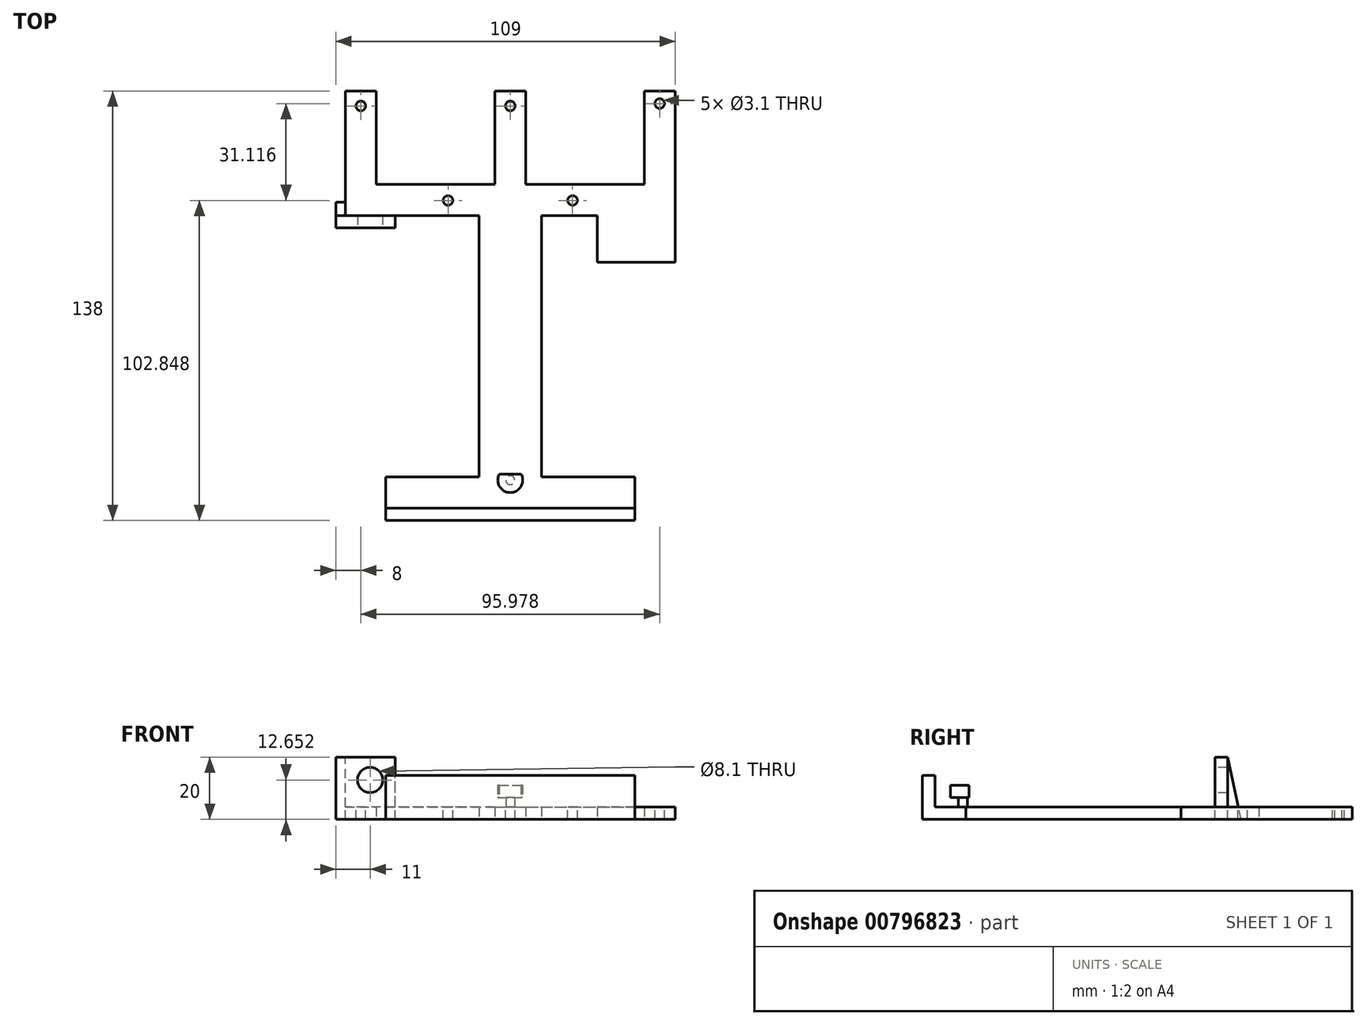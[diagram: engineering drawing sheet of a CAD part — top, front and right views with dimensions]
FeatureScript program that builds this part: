
annotation { "Feature Type Name" : "Feature", "Feature Type Description" : "" }
export const myFeature = defineFeature(function(context is Context, id is Id, definition is map)
    precondition{}
    {
        {
            var Q0;
            Q0=qCreatedBy(makeId("Top.planeOp"),FACE);
            var sketch = newSketch(context, id + "F0", { "sketchPlane" : qUnion([Q0])});
            skLineSegment(sketch, "E0.bottom", {"start": v(-10, 52) * mm, "end": v(10, 52) * mm});
            skLineSegment(sketch, "E0.top", {"start": v(-10, -52) * mm, "end": v(10, -52) * mm});
            skLineSegment(sketch, "E0.left", {"start": v(-10, 52) * mm, "end": v(-10, -52) * mm});
            skLineSegment(sketch, "E0.right", {"start": v(10, 52) * mm, "end": v(10, -52) * mm});
            skPoint(sketch, "E0.middle", {"position": v(0, 0) * mm});
            skLineSegment(sketch, "E1.bottom", {"start": v(10, 52) * mm, "end": v(53, 52) * mm});
            skLineSegment(sketch, "E1.top", {"start": v(10, 42) * mm, "end": v(53, 42) * mm});
            skLineSegment(sketch, "E1.left", {"start": v(10, 52) * mm, "end": v(10, 42) * mm});
            skLineSegment(sketch, "E1.right", {"start": v(53, 52) * mm, "end": v(53, 42) * mm});
            skLineSegment(sketch, "E2.bottom", {"start": v(-10, 52) * mm, "end": v(-53, 52) * mm});
            skLineSegment(sketch, "E2.top", {"start": v(-10, 42) * mm, "end": v(-53, 42) * mm});
            skLineSegment(sketch, "E2.left", {"start": v(-10, 52) * mm, "end": v(-10, 42) * mm});
            skLineSegment(sketch, "E2.right", {"start": v(-53, 52) * mm, "end": v(-53, 42) * mm});
            skLineSegment(sketch, "E3.bottom", {"start": v(10, -52) * mm, "end": v(40, -52) * mm});
            skLineSegment(sketch, "E3.top", {"start": v(10, -42) * mm, "end": v(40, -42) * mm});
            skLineSegment(sketch, "E3.left", {"start": v(10, -52) * mm, "end": v(10, -42) * mm});
            skLineSegment(sketch, "E3.right", {"start": v(40, -52) * mm, "end": v(40, -42) * mm});
            skLineSegment(sketch, "E4.bottom", {"start": v(-10, -52) * mm, "end": v(-40, -52) * mm});
            skLineSegment(sketch, "E4.top", {"start": v(-10, -42) * mm, "end": v(-40, -42) * mm});
            skLineSegment(sketch, "E4.left", {"start": v(-10, -52) * mm, "end": v(-10, -42) * mm});
            skLineSegment(sketch, "E4.right", {"start": v(-40, -52) * mm, "end": v(-40, -42) * mm});
            skLineSegment(sketch, "E5.bottom", {"start": v(-53, 52) * mm, "end": v(53, 52) * mm});
            skLineSegment(sketch, "E5.top", {"start": v(-53, 82) * mm, "end": v(53, 82) * mm});
            skLineSegment(sketch, "E5.left", {"start": v(-53, 52) * mm, "end": v(-53, 82) * mm});
            skLineSegment(sketch, "E5.right", {"start": v(53, 52) * mm, "end": v(53, 82) * mm});
            skLineSegment(sketch, "E6.bottom", {"start": v(53, 42) * mm, "end": v(28, 42) * mm});
            skLineSegment(sketch, "E6.top", {"start": v(53, 27) * mm, "end": v(28, 27) * mm});
            skLineSegment(sketch, "E6.left", {"start": v(53, 42) * mm, "end": v(53, 27) * mm});
            skLineSegment(sketch, "E6.right", {"start": v(28, 42) * mm, "end": v(28, 27) * mm});
            skLineSegment(sketch, "E7.bottom", {"start": v(-53, 52) * mm, "end": v(-43, 52) * mm});
            skLineSegment(sketch, "E7.top", {"start": v(-53, 82) * mm, "end": v(-43, 82) * mm});
            skLineSegment(sketch, "E7.right", {"start": v(-43, 52) * mm, "end": v(-43, 82) * mm});
            skLineSegment(sketch, "E8.bottom", {"start": v(53, 52) * mm, "end": v(43, 52) * mm});
            skLineSegment(sketch, "E8.top", {"start": v(53, 82) * mm, "end": v(43, 82) * mm});
            skLineSegment(sketch, "E8.right", {"start": v(43, 52) * mm, "end": v(43, 82) * mm});
            skLineSegment(sketch, "E9.bottom", {"start": v(0, 52) * mm, "end": v(5, 52) * mm});
            skLineSegment(sketch, "E9.top", {"start": v(0, 82) * mm, "end": v(5, 82) * mm});
            skLineSegment(sketch, "E9.left", {"start": v(0, 52) * mm, "end": v(0, 82) * mm});
            skLineSegment(sketch, "E9.right", {"start": v(5, 52) * mm, "end": v(5, 82) * mm});
            skLineSegment(sketch, "E10.bottom", {"start": v(0, 52) * mm, "end": v(-5, 52) * mm});
            skLineSegment(sketch, "E10.top", {"start": v(0, 82) * mm, "end": v(-5, 82) * mm});
            skLineSegment(sketch, "E10.right", {"start": v(-5, 52) * mm, "end": v(-5, 82) * mm});
            skSolve(sketch);
        }
        {
            var Q0;
            {var subQ0=sQuery(id+"F0.wireOp",EDGE,"E5.left");Q0=makeQuery(id+"F0.imprint","IMPRINT",FACE,{"disambiguationData":[TD([[makeQuery(id+"F0.imprint","IMPRINT",EDGE,{"derivedFrom":subQ0}),-1.0]])]});}
            var Q1;
            {var subQ0=sQuery(id+"F0.wireOp",EDGE,"E2.top");Q1=makeQuery(id+"F0.imprint","IMPRINT",FACE,{"disambiguationData":[TD([[makeQuery(id+"F0.imprint","IMPRINT",EDGE,{"derivedFrom":subQ0}),-1.0]])]});}
            var Q2;
            {var subQ2=sQuery(id+"F0.wireOp",EDGE,"E9.left");Q2=makeQuery(id+"F0.imprint","IMPRINT",FACE,{"disambiguationData":[TD([[makeQuery(id+"F0.imprint","IMPRINT",EDGE,{"derivedFrom":subQ2}),1.0]])]});}
            var Q3;
            {var subQ2=sQuery(id+"F0.wireOp",EDGE,"E9.left");Q3=makeQuery(id+"F0.imprint","IMPRINT",FACE,{"disambiguationData":[TD([[makeQuery(id+"F0.imprint","IMPRINT",EDGE,{"derivedFrom":subQ2}),-1.0]])]});}
            var Q4;
            {var subQ6=sQuery(id+"F0.wireOp",EDGE,"E0.top");Q4=makeQuery(id+"F0.imprint","IMPRINT",FACE,{"disambiguationData":[TD([[makeQuery(id+"F0.imprint","IMPRINT",EDGE,{"derivedFrom":subQ6}),1.0]])]});}
            var Q5;
            {var subQ0=sQuery(id+"F0.wireOp",EDGE,"E4.bottom");Q5=makeQuery(id+"F0.imprint","IMPRINT",FACE,{"disambiguationData":[TD([[makeQuery(id+"F0.imprint","IMPRINT",EDGE,{"derivedFrom":subQ0}),-1.0]])]});}
            var Q6;
            {var subQ0=sQuery(id+"F0.wireOp",EDGE,"E3.bottom");Q6=makeQuery(id+"F0.imprint","IMPRINT",FACE,{"disambiguationData":[TD([[makeQuery(id+"F0.imprint","IMPRINT",EDGE,{"derivedFrom":subQ0}),1.0]])]});}
            var Q7;
            Q7=makeQuery(id+"F0.imprint","IMPRINT",FACE,{"disambiguationData":[TD([[makeQuery(id+"F0.imprint","IMPRINT",EDGE,{"derivedFrom":sQuery(id+"F0.wireOp",EDGE,"E6.top")}),-1.0]])]});
            var Q8;
            {var subQ1=sQuery(id+"F0.wireOp",EDGE,"E1.bottom");Q8=makeQuery(id+"F0.imprint","IMPRINT",FACE,{"disambiguationData":[TD([[makeQuery(id+"F0.imprint","IMPRINT",EDGE,{"derivedFrom":subQ1}),-1.0]])]});}
            var Q9;
            {var subQ0=sQuery(id+"F0.wireOp",EDGE,"E5.right");Q9=makeQuery(id+"F0.imprint","IMPRINT",FACE,{"disambiguationData":[TD([[makeQuery(id+"F0.imprint","IMPRINT",EDGE,{"derivedFrom":subQ0}),1.0]])]});}
            var Q10;
            {var subQ2=sQuery(id+"F0.wireOp",EDGE,"E1.right");Q10=makeQuery(id+"F0.imprint","IMPRINT",FACE,{"disambiguationData":[TD([[makeQuery(id+"F0.imprint","IMPRINT",EDGE,{"derivedFrom":subQ2}),-1.0]])]});}
            extrude(context, id + "F1", {"entities" : qUnion([Q0, Q1, Q2, Q3, Q4, Q5, Q6, Q7, Q8, Q9, Q10]), "depth" : 4 * mm, "offsetDistance" : 25 * mm});
        }
        {
            var Q0;
            Q0=makeQuery(id+"F1.opExtrude","SWEPT_FACE",FACE,{"disambiguationData":[OSD([sQuery(id+"F0.wireOp",EDGE,"E2.top")])]});
            var sketch = newSketch(context, id + "F2", { "sketchPlane" : qUnion([Q0])});
            skLineSegment(sketch, "E11.bottom", {"start": v(-53, 0) * mm, "end": v(-37, 0) * mm});
            skLineSegment(sketch, "E11.top", {"start": v(-53, 20) * mm, "end": v(-37, 20) * mm});
            skLineSegment(sketch, "E11.left", {"start": v(-53, 0) * mm, "end": v(-53, 20) * mm});
            skLineSegment(sketch, "E11.right", {"start": v(-37, 0) * mm, "end": v(-37, 20) * mm});
            skSolve(sketch);
        }
        {
            var Q0;
            {var subQ0=sQuery(id+"F2.wireOp",EDGE,"E11.top");Q0=makeQuery(id+"F2.imprint","IMPRINT",FACE,{"disambiguationData":[TD([[makeQuery(id+"F2.imprint","IMPRINT",EDGE,{"derivedFrom":subQ0}),-1.0]])]});}
            var Q1;
            {var subQ0=sQuery(id+"F2.wireOp",EDGE,"E11.bottom");Q1=makeQuery(id+"F2.imprint","IMPRINT",FACE,{"disambiguationData":[TD([[makeQuery(id+"F2.imprint","IMPRINT",EDGE,{"derivedFrom":subQ0}),-1.0]])]});}
            extrude(context, id + "F3", {"entities" : qUnion([Q0, Q1]), "operationType" : NewBodyOperationType.ADD, "depth" : 4 * mm, "offsetDistance" : 25 * mm});
        }
        {
            var Q0;
            Q0=makeQuery(id+"F3.opExtrude","CAP_FACE",FACE,{"disambiguationData":[OSD([sQuery(id+"F2.wireOp",EDGE,"E11.bottom"),sQuery(id+"F2.wireOp",EDGE,"E11.top"),sQuery(id+"F2.wireOp",EDGE,"E11.left"),sQuery(id+"F2.wireOp",EDGE,"E11.right")])],"isStart":false});
            var sketch = newSketch(context, id + "F4", { "sketchPlane" : qUnion([Q0])});
            skCircle(sketch, "E12", {"center": v(-45, 12.65) * mm, "radius": 4.07 * mm});
            skPoint(sketch, "E12.centerSnap0", {"position": v(-45, 20) * mm});
            skSolve(sketch);
        }
        {
            var Q0;
            Q0=sQuery(id+"F4.wireOp",VERTEX,"E12.center");
            var Q1;
            Q1=makeQuery(id+"F1.opExtrude","SWEPT_BODY",BODY,{"disambiguationData":[OSD([sQuery(id+"F0.wireOp",EDGE,"E0.bottom"),sQuery(id+"F0.wireOp",EDGE,"E0.top"),sQuery(id+"F0.wireOp",EDGE,"E0.left"),sQuery(id+"F0.wireOp",EDGE,"E0.right"),sQuery(id+"F0.wireOp",EDGE,"E1.bottom"),sQuery(id+"F0.wireOp",EDGE,"E1.top"),sQuery(id+"F0.wireOp",EDGE,"E1.right"),sQuery(id+"F0.wireOp",EDGE,"E2.bottom"),sQuery(id+"F0.wireOp",EDGE,"E2.top"),sQuery(id+"F0.wireOp",EDGE,"E2.right"),sQuery(id+"F0.wireOp",EDGE,"E3.bottom"),sQuery(id+"F0.wireOp",EDGE,"E3.top"),sQuery(id+"F0.wireOp",EDGE,"E3.right"),sQuery(id+"F0.wireOp",EDGE,"E4.bottom"),sQuery(id+"F0.wireOp",EDGE,"E4.top"),sQuery(id+"F0.wireOp",EDGE,"E4.right"),sQuery(id+"F0.wireOp",EDGE,"E5.top"),sQuery(id+"F0.wireOp",EDGE,"E5.left"),sQuery(id+"F0.wireOp",EDGE,"E5.right"),sQuery(id+"F0.wireOp",EDGE,"E6.top"),sQuery(id+"F0.wireOp",EDGE,"E6.left"),sQuery(id+"F0.wireOp",EDGE,"E6.right"),sQuery(id+"F0.wireOp",EDGE,"E7.right"),sQuery(id+"F0.wireOp",EDGE,"E8.right"),sQuery(id+"F0.wireOp",EDGE,"E9.right"),sQuery(id+"F0.wireOp",EDGE,"E10.right")])]});
            hole(context, id + "F5", {"style" : HoleStyle.SIMPLE, "endStyle" : HoleEndStyle.THROUGH, "holeDiameter" : 8.1 * mm, "majorDiameter" : 5 * mm, "isTappedThrough" : true, "tappedDepth" : 12 * mm, "tapClearance" : 3, "locations" : qUnion([Q0]), "scope" : qUnion([Q1])});
        }
        {
            var Q0;
            Q0=makeQuery(id+"F3.boolean.opBoolean","MERGE",FACE,{"derivedFrom":[makeQuery(id+"F1.opExtrude","SWEPT_FACE",FACE,{"disambiguationData":[OSD([sQuery(id+"F0.wireOp",EDGE,"E2.right"),sQuery(id+"F0.wireOp",EDGE,"E5.left")])]}),makeQuery(id+"F3.opExtrude","SWEPT_FACE",FACE,{"disambiguationData":[OSD([sQuery(id+"F2.wireOp",EDGE,"E11.left")])]})]});
            var sketch = newSketch(context, id + "F6", { "sketchPlane" : qUnion([Q0])});
            skLineSegment(sketch, "E13", {"start": v(-46.34, 0) * mm, "end": v(-42, 20) * mm});
            skLineSegment(sketch, "E14", {"start": v(-42, 20) * mm, "end": v(-38, 20) * mm});
            skLineSegment(sketch, "E15", {"start": v(-38, 20) * mm, "end": v(-38, 0) * mm});
            skLineSegment(sketch, "E16", {"start": v(-38, 0) * mm, "end": v(-46.34, 0) * mm});
            skSolve(sketch);
        }
        {
            var Q0;
            {var subQ1=makeQuery(id+"F3.opExtrude","CAP_EDGE",EDGE,{"disambiguationData":[OSD([sQuery(id+"F2.wireOp",EDGE,"E11.left")])],"isStart":true});Q0=makeQuery(id+"F6.imprint","IMPRINT",FACE,{"disambiguationData":[TD([[makeQuery(id+"F6.imprint","IMPRINT",EDGE,{"derivedFrom":subQ1}),1.0]])]});}
            var Q1;
            Q1=makeQuery(id+"F6.imprint","IMPRINT",FACE,{"disambiguationData":[TD([[makeQuery(id+"F6.imprint","IMPRINT",EDGE,{"derivedFrom":sQuery(id+"F6.wireOp",EDGE,"E14")}),1.0]])]});
            extrude(context, id + "F7", {"entities" : qUnion([Q0, Q1]), "operationType" : NewBodyOperationType.ADD, "depth" : 3 * mm, "offsetDistance" : 25 * mm});
        }
        {
            var Q0;
            Q0=makeQuery(id+"F1.opExtrude","SWEPT_FACE",FACE,{"disambiguationData":[OSD([sQuery(id+"F0.wireOp",EDGE,"E0.top"),sQuery(id+"F0.wireOp",EDGE,"E3.bottom"),sQuery(id+"F0.wireOp",EDGE,"E4.bottom")])]});
            var sketch = newSketch(context, id + "F8", { "sketchPlane" : qUnion([Q0])});
            skLineSegment(sketch, "E17.bottom", {"start": v(-40, 0) * mm, "end": v(40, 0) * mm});
            skLineSegment(sketch, "E17.top", {"start": v(-40, 14.08) * mm, "end": v(40, 14.08) * mm});
            skLineSegment(sketch, "E17.left", {"start": v(-40, 0) * mm, "end": v(-40, 14.08) * mm});
            skLineSegment(sketch, "E17.right", {"start": v(40, 0) * mm, "end": v(40, 14.08) * mm});
            skSolve(sketch);
        }
        {
            var Q0;
            {var subQ0=sQuery(id+"F8.wireOp",EDGE,"E17.top");Q0=makeQuery(id+"F8.imprint","IMPRINT",FACE,{"disambiguationData":[TD([[makeQuery(id+"F8.imprint","IMPRINT",EDGE,{"derivedFrom":subQ0}),-1.0]])]});}
            var Q1;
            {var subQ0=sQuery(id+"F8.wireOp",EDGE,"E17.bottom");Q1=makeQuery(id+"F8.imprint","IMPRINT",FACE,{"disambiguationData":[TD([[makeQuery(id+"F8.imprint","IMPRINT",EDGE,{"derivedFrom":subQ0}),1.0]])]});}
            extrude(context, id + "F9", {"entities" : qUnion([Q0, Q1]), "operationType" : NewBodyOperationType.ADD, "depth" : 4 * mm, "offsetDistance" : 25 * mm});
        }
        {
            var Q0;
            Q0=makeQuery(id+"F1.opExtrude","CAP_FACE",FACE,{"disambiguationData":[OSD([sQuery(id+"F0.wireOp",EDGE,"E0.bottom"),sQuery(id+"F0.wireOp",EDGE,"E0.top"),sQuery(id+"F0.wireOp",EDGE,"E0.left"),sQuery(id+"F0.wireOp",EDGE,"E0.right"),sQuery(id+"F0.wireOp",EDGE,"E1.bottom"),sQuery(id+"F0.wireOp",EDGE,"E1.top"),sQuery(id+"F0.wireOp",EDGE,"E1.right"),sQuery(id+"F0.wireOp",EDGE,"E2.bottom"),sQuery(id+"F0.wireOp",EDGE,"E2.top"),sQuery(id+"F0.wireOp",EDGE,"E2.right"),sQuery(id+"F0.wireOp",EDGE,"E3.bottom"),sQuery(id+"F0.wireOp",EDGE,"E3.top"),sQuery(id+"F0.wireOp",EDGE,"E3.right"),sQuery(id+"F0.wireOp",EDGE,"E4.bottom"),sQuery(id+"F0.wireOp",EDGE,"E4.top"),sQuery(id+"F0.wireOp",EDGE,"E4.right"),sQuery(id+"F0.wireOp",EDGE,"E5.top"),sQuery(id+"F0.wireOp",EDGE,"E5.left"),sQuery(id+"F0.wireOp",EDGE,"E5.right"),sQuery(id+"F0.wireOp",EDGE,"E6.top"),sQuery(id+"F0.wireOp",EDGE,"E6.left"),sQuery(id+"F0.wireOp",EDGE,"E6.right"),sQuery(id+"F0.wireOp",EDGE,"E7.right"),sQuery(id+"F0.wireOp",EDGE,"E8.right"),sQuery(id+"F0.wireOp",EDGE,"E9.right"),sQuery(id+"F0.wireOp",EDGE,"E10.right")])],"isStart":false});
            var sketch = newSketch(context, id + "F10", { "sketchPlane" : qUnion([Q0])});
            skCircle(sketch, "E18", {"center": v(-48, 77.2) * mm, "radius": 1.55 * mm});
            skPoint(sketch, "E18.centerSnap0", {"position": v(-48, 82) * mm});
            skCircle(sketch, "E19", {"center": v(0, 77.2) * mm, "radius": 1.55 * mm});
            skCircle(sketch, "E20", {"center": v(71.87, 77.2) * mm, "radius": 1.55 * mm});
            skCircle(sketch, "E21", {"center": v(20, 46.85) * mm, "radius": 1.55 * mm});
            skCircle(sketch, "E22", {"center": v(-20, 46.85) * mm, "radius": 1.55 * mm});
            skCircle(sketch, "E23", {"center": v(0, -43.15) * mm, "radius": 1.45 * mm});
            skSolve(sketch);
        }
        {
            var Q0;
            Q0=sQuery(id+"F10.wireOp",VERTEX,"E22.center");
            var Q1;
            Q1=sQuery(id+"F10.wireOp",VERTEX,"E21.center");
            var Q2;
            Q2=sQuery(id+"F10.wireOp",VERTEX,"E18.center");
            var Q3;
            Q3=sQuery(id+"F10.wireOp",VERTEX,"E19.center");
            var Q4;
            Q4=sQuery(id+"F10.wireOp",VERTEX,"E20.center");
            var Q5;
            Q5=makeQuery(id+"F1.opExtrude","SWEPT_BODY",BODY,{"disambiguationData":[OSD([sQuery(id+"F0.wireOp",EDGE,"E0.bottom"),sQuery(id+"F0.wireOp",EDGE,"E0.top"),sQuery(id+"F0.wireOp",EDGE,"E0.left"),sQuery(id+"F0.wireOp",EDGE,"E0.right"),sQuery(id+"F0.wireOp",EDGE,"E1.bottom"),sQuery(id+"F0.wireOp",EDGE,"E1.top"),sQuery(id+"F0.wireOp",EDGE,"E1.right"),sQuery(id+"F0.wireOp",EDGE,"E2.bottom"),sQuery(id+"F0.wireOp",EDGE,"E2.top"),sQuery(id+"F0.wireOp",EDGE,"E2.right"),sQuery(id+"F0.wireOp",EDGE,"E3.bottom"),sQuery(id+"F0.wireOp",EDGE,"E3.top"),sQuery(id+"F0.wireOp",EDGE,"E3.right"),sQuery(id+"F0.wireOp",EDGE,"E4.bottom"),sQuery(id+"F0.wireOp",EDGE,"E4.top"),sQuery(id+"F0.wireOp",EDGE,"E4.right"),sQuery(id+"F0.wireOp",EDGE,"E5.top"),sQuery(id+"F0.wireOp",EDGE,"E5.left"),sQuery(id+"F0.wireOp",EDGE,"E5.right"),sQuery(id+"F0.wireOp",EDGE,"E6.top"),sQuery(id+"F0.wireOp",EDGE,"E6.left"),sQuery(id+"F0.wireOp",EDGE,"E6.right"),sQuery(id+"F0.wireOp",EDGE,"E7.right"),sQuery(id+"F0.wireOp",EDGE,"E8.right"),sQuery(id+"F0.wireOp",EDGE,"E9.right"),sQuery(id+"F0.wireOp",EDGE,"E10.right")])]});
            hole(context, id + "F11", {"style" : HoleStyle.SIMPLE, "endStyle" : HoleEndStyle.THROUGH, "holeDiameter" : 3.1 * mm, "majorDiameter" : 5 * mm, "isTappedThrough" : true, "tappedDepth" : 12 * mm, "tapClearance" : 3, "locations" : qUnion([Q0, Q1, Q2, Q3, Q4]), "scope" : qUnion([Q5])});
        }
        {
            var Q0;
            Q0=makeQuery(id+"F1.opExtrude","CAP_FACE",FACE,{"disambiguationData":[OSD([sQuery(id+"F0.wireOp",EDGE,"E0.bottom"),sQuery(id+"F0.wireOp",EDGE,"E0.top"),sQuery(id+"F0.wireOp",EDGE,"E0.left"),sQuery(id+"F0.wireOp",EDGE,"E0.right"),sQuery(id+"F0.wireOp",EDGE,"E1.bottom"),sQuery(id+"F0.wireOp",EDGE,"E1.top"),sQuery(id+"F0.wireOp",EDGE,"E1.right"),sQuery(id+"F0.wireOp",EDGE,"E2.bottom"),sQuery(id+"F0.wireOp",EDGE,"E2.top"),sQuery(id+"F0.wireOp",EDGE,"E2.right"),sQuery(id+"F0.wireOp",EDGE,"E3.bottom"),sQuery(id+"F0.wireOp",EDGE,"E3.top"),sQuery(id+"F0.wireOp",EDGE,"E3.right"),sQuery(id+"F0.wireOp",EDGE,"E4.bottom"),sQuery(id+"F0.wireOp",EDGE,"E4.top"),sQuery(id+"F0.wireOp",EDGE,"E4.right"),sQuery(id+"F0.wireOp",EDGE,"E5.top"),sQuery(id+"F0.wireOp",EDGE,"E5.left"),sQuery(id+"F0.wireOp",EDGE,"E5.right"),sQuery(id+"F0.wireOp",EDGE,"E6.top"),sQuery(id+"F0.wireOp",EDGE,"E6.left"),sQuery(id+"F0.wireOp",EDGE,"E6.right"),sQuery(id+"F0.wireOp",EDGE,"E7.right"),sQuery(id+"F0.wireOp",EDGE,"E8.right"),sQuery(id+"F0.wireOp",EDGE,"E9.right"),sQuery(id+"F0.wireOp",EDGE,"E10.right")])],"isStart":false});
            var sketch = newSketch(context, id + "F12", { "sketchPlane" : qUnion([Q0])});
            skCircle(sketch, "E24", {"center": v(0, -43) * mm, "radius": 1.45 * mm});
            skSolve(sketch);
        }
        {
            var Q0;
            Q0=makeQuery(id+"F12.imprint","IMPRINT",FACE,{"disambiguationData":[TD([[makeQuery(id+"F12.imprint","IMPRINT",EDGE,{"derivedFrom":sQuery(id+"F12.wireOp",EDGE,"E24")}),1.0]])]});
            extrude(context, id + "F13", {"entities" : qUnion([Q0]), "operationType" : NewBodyOperationType.ADD, "depth" : 3 * mm, "offsetDistance" : 25 * mm});
        }
        {
            var Q0;
            Q0=makeQuery(id+"F13.opExtrude","CAP_FACE",FACE,{"disambiguationData":[OSD([sQuery(id+"F12.wireOp",EDGE,"E24")])],"isStart":false});
            var sketch = newSketch(context, id + "F14", { "sketchPlane" : qUnion([Q0])});
            skCircle(sketch, "E25", {"center": v(0, -43) * mm, "radius": 4 * mm});
            skLineSegment(sketch, "E26", {"start": v(-3.5, -41.06) * mm, "end": v(3.5, -41.06) * mm});
            skSolve(sketch);
        }
        {
            var Q0;
            Q0=makeQuery(id+"F14.imprint","IMPRINT",FACE,{"disambiguationData":[TD([[makeQuery(id+"F14.imprint","IMPRINT",EDGE,{"derivedFrom":makeQuery(id+"F13.opExtrude","CAP_EDGE",EDGE,{"disambiguationData":[OSD([sQuery(id+"F12.wireOp",EDGE,"E24")])],"isStart":false})}),1.0]])]});
            var Q1;
            {var subQ0=sQuery(id+"F14.wireOp",EDGE,"E26");Q1=makeQuery(id+"F14.imprint","IMPRINT",FACE,{"disambiguationData":[TD([[makeQuery(id+"F14.imprint","IMPRINT",EDGE,{"derivedFrom":subQ0}),-1.0]])]});}
            extrude(context, id + "F15", {"entities" : qUnion([Q0, Q1]), "operationType" : NewBodyOperationType.ADD, "depth" : 4 * mm, "offsetDistance" : 25 * mm});
        }
        {
            var Q0;
            Q0=makeQuery(id+"F1.opExtrude","CAP_FACE",FACE,{"disambiguationData":[OSD([sQuery(id+"F0.wireOp",EDGE,"E0.bottom"),sQuery(id+"F0.wireOp",EDGE,"E0.top"),sQuery(id+"F0.wireOp",EDGE,"E0.left"),sQuery(id+"F0.wireOp",EDGE,"E0.right"),sQuery(id+"F0.wireOp",EDGE,"E1.bottom"),sQuery(id+"F0.wireOp",EDGE,"E1.top"),sQuery(id+"F0.wireOp",EDGE,"E1.right"),sQuery(id+"F0.wireOp",EDGE,"E2.bottom"),sQuery(id+"F0.wireOp",EDGE,"E2.top"),sQuery(id+"F0.wireOp",EDGE,"E2.right"),sQuery(id+"F0.wireOp",EDGE,"E3.bottom"),sQuery(id+"F0.wireOp",EDGE,"E3.top"),sQuery(id+"F0.wireOp",EDGE,"E3.right"),sQuery(id+"F0.wireOp",EDGE,"E4.bottom"),sQuery(id+"F0.wireOp",EDGE,"E4.top"),sQuery(id+"F0.wireOp",EDGE,"E4.right"),sQuery(id+"F0.wireOp",EDGE,"E5.top"),sQuery(id+"F0.wireOp",EDGE,"E5.left"),sQuery(id+"F0.wireOp",EDGE,"E5.right"),sQuery(id+"F0.wireOp",EDGE,"E6.top"),sQuery(id+"F0.wireOp",EDGE,"E6.left"),sQuery(id+"F0.wireOp",EDGE,"E6.right"),sQuery(id+"F0.wireOp",EDGE,"E7.right"),sQuery(id+"F0.wireOp",EDGE,"E8.right"),sQuery(id+"F0.wireOp",EDGE,"E9.right"),sQuery(id+"F0.wireOp",EDGE,"E10.right")])],"isStart":false});
            var sketch = newSketch(context, id + "F16", { "sketchPlane" : qUnion([Q0])});
            skCircle(sketch, "E27", {"center": v(47.98, 77.96) * mm, "radius": 1.6 * mm});
            skSolve(sketch);
        }
        {
            var Q0;
            Q0=sQuery(id+"F16.wireOp",VERTEX,"E27.center");
            var Q1;
            Q1=makeQuery(id+"F1.opExtrude","SWEPT_BODY",BODY,{"disambiguationData":[OSD([sQuery(id+"F0.wireOp",EDGE,"E0.bottom"),sQuery(id+"F0.wireOp",EDGE,"E0.top"),sQuery(id+"F0.wireOp",EDGE,"E0.left"),sQuery(id+"F0.wireOp",EDGE,"E0.right"),sQuery(id+"F0.wireOp",EDGE,"E1.bottom"),sQuery(id+"F0.wireOp",EDGE,"E1.top"),sQuery(id+"F0.wireOp",EDGE,"E1.right"),sQuery(id+"F0.wireOp",EDGE,"E2.bottom"),sQuery(id+"F0.wireOp",EDGE,"E2.top"),sQuery(id+"F0.wireOp",EDGE,"E2.right"),sQuery(id+"F0.wireOp",EDGE,"E3.bottom"),sQuery(id+"F0.wireOp",EDGE,"E3.top"),sQuery(id+"F0.wireOp",EDGE,"E3.right"),sQuery(id+"F0.wireOp",EDGE,"E4.bottom"),sQuery(id+"F0.wireOp",EDGE,"E4.top"),sQuery(id+"F0.wireOp",EDGE,"E4.right"),sQuery(id+"F0.wireOp",EDGE,"E5.top"),sQuery(id+"F0.wireOp",EDGE,"E5.left"),sQuery(id+"F0.wireOp",EDGE,"E5.right"),sQuery(id+"F0.wireOp",EDGE,"E6.top"),sQuery(id+"F0.wireOp",EDGE,"E6.left"),sQuery(id+"F0.wireOp",EDGE,"E6.right"),sQuery(id+"F0.wireOp",EDGE,"E7.right"),sQuery(id+"F0.wireOp",EDGE,"E8.right"),sQuery(id+"F0.wireOp",EDGE,"E9.right"),sQuery(id+"F0.wireOp",EDGE,"E10.right")])]});
            hole(context, id + "F17", {"style" : HoleStyle.SIMPLE, "endStyle" : HoleEndStyle.THROUGH, "holeDiameter" : 3.1 * mm, "majorDiameter" : 5 * mm, "isTappedThrough" : true, "tappedDepth" : 12 * mm, "tapClearance" : 3, "locations" : qUnion([Q0]), "scope" : qUnion([Q1])});
        }
    });
